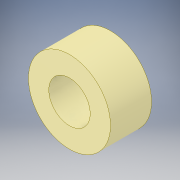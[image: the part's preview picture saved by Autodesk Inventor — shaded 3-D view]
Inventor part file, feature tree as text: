
AUTODESK INVENTOR PART (.ipt)
format: ipt  version: 2017 (Build 210142000, 142)  size: 98,304 bytes
history: native  units: in
note: dims shown in document units (in); Inventor stores cm internally (conversion verified against a paired STEP export)
features: extrude x1, sketch x1
ambient origin geometry x8: Origin, YZ Plane, XZ Plane, XY Plane, X Axis, Y Axis, Z Axis, Center Point
bodies: Solid1 (feature_tree)
feature tree (2):
  extrude  "Extrusion1"  Depth=0.5in
  sketch  "Sketch1"  dims[d0=0.505in d1=1.0in d2=0.5in d3=0.0in]
